# Revit family: VB Series Valves Boxes -  Max Jumbo Valve Box
name_source: partatom
category: Acessórios do tubo
units: mm (PartAtom-declared; Revit-internal decimal feet)

## family parameters
Com base no plano de trabalho = Não
Compartilhado = Não
Corte com vazios quando carregada = Não
Cota do conector redondo = Utilizar diâmetro
Número OmniClass = 23.60.00.00
Sempre na vertical = Sim
Tipo de parte = Normal
Título OmniClass = General Purpose: Services

## types (1)
- Max Jumbo Valve Box
    DDT1 = 0
    DDT2 = 34
    DDT3 = 51
    DDT4 = 0
    DDT5 = 2
    DDT6 = 2
    DDT7 = 4
    DDT8 = 3
    Descrição = VB Series Valves Boxes - Max Jumbo Valve Box
    Elevação padrão = 0
    Height = 46
    Length = 102
    Modelo = VBMAXH
    Plastic 1 = Black
    Plastic 2 = Green 2
    R = 4
    RainBird: Code = A61483
    RainBird: Description = VB Series Valves Boxes - Max Jumbo Valve Box
    RainBird: Product Link = https://www.rainbird.com
    SupportProjetos: Level of Detail = LOD300
    SupportProjetos: Reviw = R00
    URL = https://www.rainbird.com
    Width = 69
    x = 7
